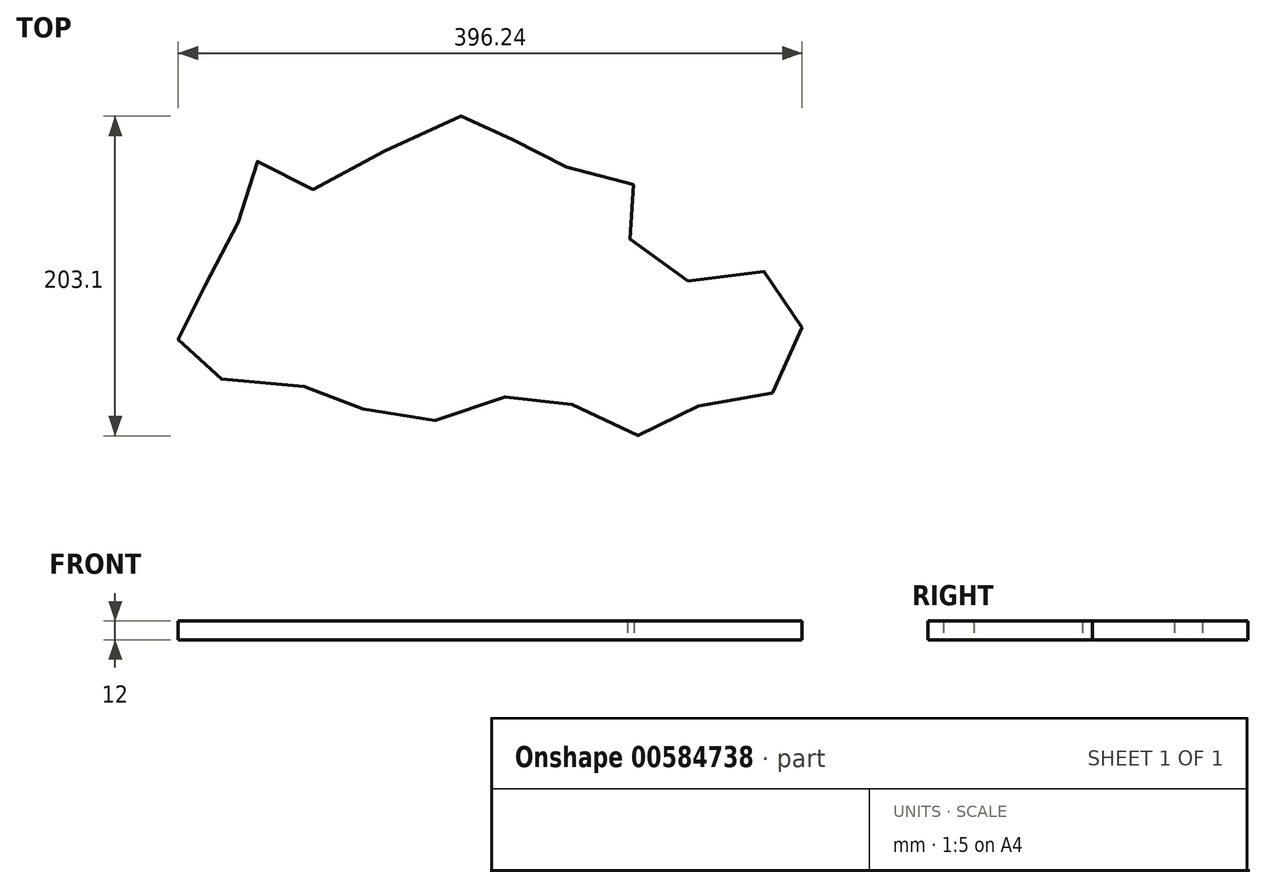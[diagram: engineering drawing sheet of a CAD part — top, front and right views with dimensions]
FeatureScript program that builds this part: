
annotation { "Feature Type Name" : "Feature", "Feature Type Description" : "" }
export const myFeature = defineFeature(function(context is Context, id is Id, definition is map)
    precondition{}
    {
        {
            var Q0;
            Q0=qCreatedBy(makeId("Top.planeOp"),FACE);
            var sketch = newSketch(context, id + "F0", { "sketchPlane" : qUnion([Q0])});
            skFitSpline(sketch, "E0", {"points": [v(-215.42, 85.17) * mm, v(-145.42, 126.02) * mm, v(-95.6, 124.12) * mm, v(-74.19, 103.84) * mm, v(-13.07, 90.07) * mm, v(-15.8, 60.4) * mm, v(24.68, 26.8) * mm, v(82.16, 29.2) * mm, v(87.87, -36.27) * mm, v(32.85, -51.35) * mm, v(-13.22, -71.35) * mm, v(-70.2, -42.85) * mm, v(-122.98, -59.16) * mm, v(-182.81, -54.6) * mm, v(-226.26, -39.2) * mm, v(-293.97, -27.47) * mm, v(-295.82, 10.38) * mm, v(-267.75, 45.95) * mm, v(-252.27, 102.6) * mm, v(-215.42, 85.17) * mm]});
            skSolve(sketch);
        }
        {
            var Q0;
            Q0=makeQuery(id+"F0.imprint","IMPRINT",FACE,{"disambiguationData":[TD([[makeQuery(id+"F0.imprint","IMPRINT",EDGE,{"derivedFrom":sQuery(id+"F0.wireOp",EDGE,"E0")}),-1.0]])]});
            extrude(context, id + "F1", {"entities" : qUnion([Q0]), "depth" : 12 * mm, "offsetDistance" : 25 * mm});
        }
    });
